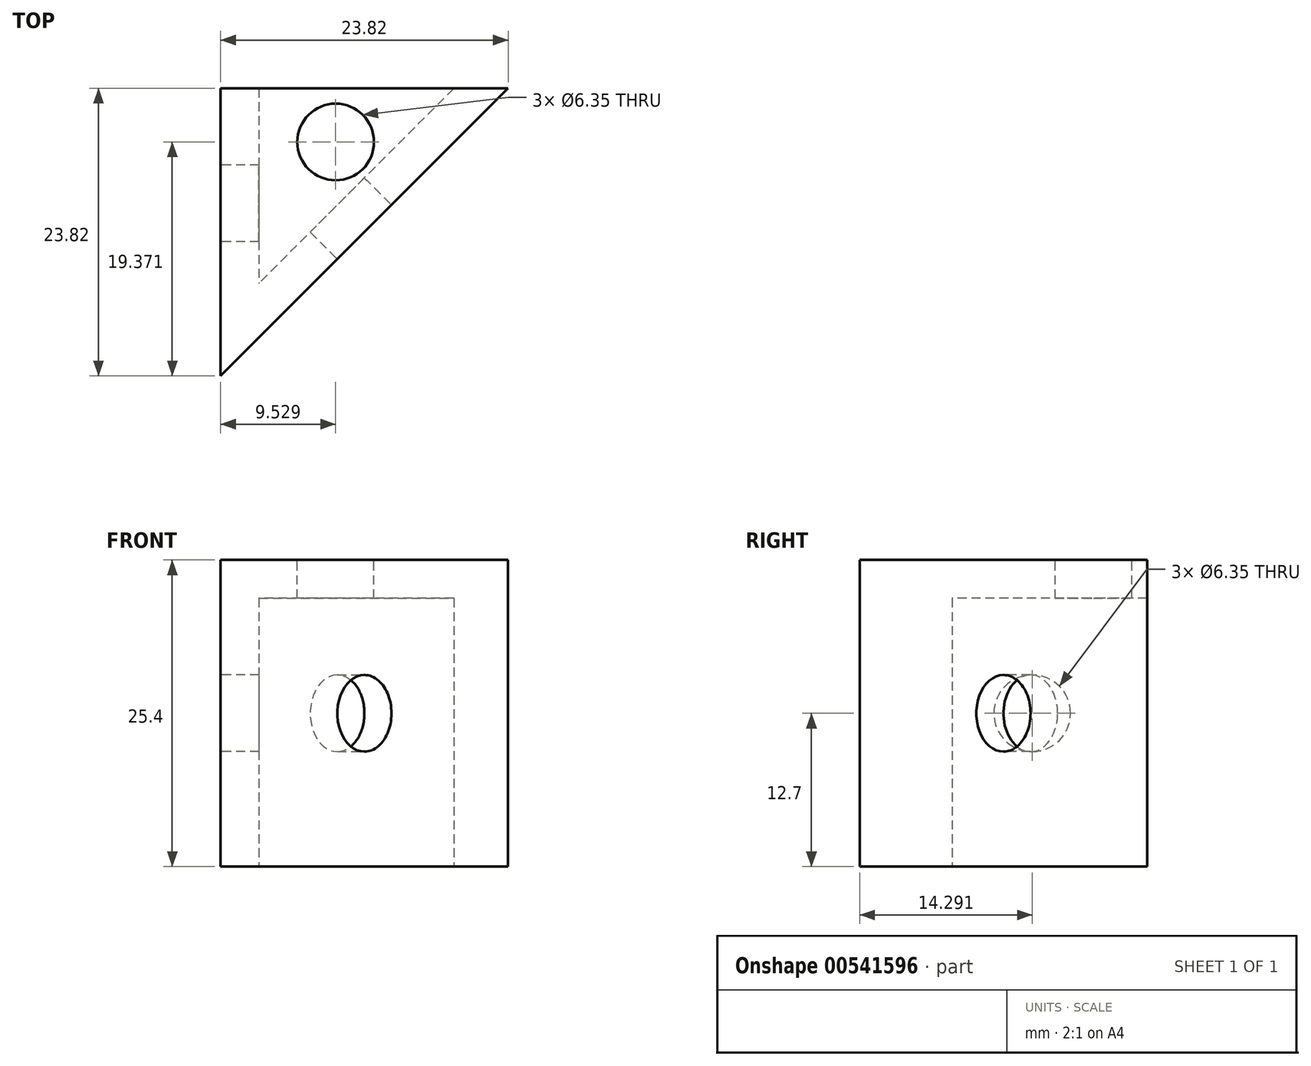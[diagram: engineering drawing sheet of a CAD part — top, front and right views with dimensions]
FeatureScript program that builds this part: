
annotation { "Feature Type Name" : "Feature", "Feature Type Description" : "" }
export const myFeature = defineFeature(function(context is Context, id is Id, definition is map)
    precondition{}
    {
        {
            var Q0;
            Q0=qCreatedBy(makeId("Top.planeOp"),FACE);
            var sketch = newSketch(context, id + "F0", { "sketchPlane" : qUnion([Q0])});
            skLineSegment(sketch, "E0.bottom", {"start": v(-11.9, 11.9) * mm, "end": v(11.9, 11.9) * mm});
            skLineSegment(sketch, "E0.top", {"start": v(-11.9, -11.9) * mm, "end": v(11.9, -11.9) * mm});
            skLineSegment(sketch, "E0.left", {"start": v(-11.9, 11.9) * mm, "end": v(-11.9, -11.9) * mm});
            skLineSegment(sketch, "E0.right", {"start": v(11.9, 11.9) * mm, "end": v(11.9, -11.9) * mm});
            skPoint(sketch, "E0.middle", {"position": v(0, 0) * mm});
            skLineSegment(sketch, "E1", {"start": v(11.9, 11.9) * mm, "end": v(-11.9, -11.9) * mm});
            skSolve(sketch);
        }
        {
            var Q0;
            Q0=makeQuery(id+"F0.imprint","IMPRINT",FACE,{"disambiguationData":[TD([[makeQuery(id+"F0.imprint","IMPRINT",EDGE,{"derivedFrom":sQuery(id+"F0.wireOp",EDGE,"E0.bottom")}),-1.0]])]});
            extrude(context, id + "F1", {"entities" : qUnion([Q0]), "depth" : 25.4 * mm, "offsetDistance" : 25.4 * mm});
        }
        {
            var Q0;
            Q0=makeQuery(id+"F1.opExtrude","SWEPT_FACE",FACE,{"disambiguationData":[OSD([sQuery(id+"F0.wireOp",EDGE,"E0.bottom")])]});
            shell(context, id + "F2", {"entities" : qUnion([Q0]), "thickness" : 3.17 * mm});
        }
        {
            var Q0;
            {var subQ0=sQuery(id+"F0.wireOp",EDGE,"E1");var subQ1=sQuery(id+"F0.wireOp",EDGE,"E0.left");var subQ2=sQuery(id+"F0.wireOp",EDGE,"E0.bottom");Q0=makeQuery(id+"F2.opShell","OFFSET_FACE",FACE,{"disambiguationData":[OSD([subQ2,subQ1,subQ0]),TDD([makeQuery(id+"F1.opExtrude","CAP_FACE",FACE,{"disambiguationData":[OSD([subQ2,subQ1,subQ0])],"isStart":true})])]});}
            extrude(context, id + "F3", {"entities" : qUnion([Q0]), "operationType" : NewBodyOperationType.REMOVE, "oppositeDirection" : true, "depth" : 25.4 * mm, "offsetDistance" : 25.4 * mm});
        }
        {
            var Q0;
            Q0=makeQuery(id+"F1.opExtrude","SWEPT_FACE",FACE,{"disambiguationData":[OSD([sQuery(id+"F0.wireOp",EDGE,"E0.left")])]});
            var sketch = newSketch(context, id + "F4", { "sketchPlane" : qUnion([Q0])});
            skCircle(sketch, "E2", {"center": v(-2.38, 12.7) * mm, "radius": 3.18 * mm});
            skSolve(sketch);
        }
        {
            var Q0;
            Q0=makeQuery(id+"F4.imprint","IMPRINT",FACE,{"disambiguationData":[TD([[makeQuery(id+"F4.imprint","IMPRINT",EDGE,{"derivedFrom":sQuery(id+"F4.wireOp",EDGE,"E2")}),1.0]])]});
            extrude(context, id + "F5", {"entities" : qUnion([Q0]), "operationType" : NewBodyOperationType.REMOVE, "oppositeDirection" : true, "depth" : 3.17 * mm, "offsetDistance" : 25.4 * mm});
        }
        {
            var Q0;
            Q0=makeQuery(id+"F1.opExtrude","CAP_FACE",FACE,{"disambiguationData":[OSD([sQuery(id+"F0.wireOp",EDGE,"E0.bottom"),sQuery(id+"F0.wireOp",EDGE,"E0.left"),sQuery(id+"F0.wireOp",EDGE,"E1")])],"isStart":false});
            var sketch = newSketch(context, id + "F6", { "sketchPlane" : qUnion([Q0])});
            skCircle(sketch, "E3", {"center": v(-2.38, 7.46) * mm, "radius": 3.18 * mm});
            skSolve(sketch);
        }
        {
            var Q0;
            {var subQ0=sQuery(id+"F6.wireOp",EDGE,"E3");var subQ1=sQuery(id+"F6.wireOp",EDGE,"HWwZXyzN-BkNU-UMwY-gXSM-99bSMozpZ1Sp");var subQ2=makeQuery(id+"F6.imprint","INTERSECT",VERTEX,{"disambiguationData":[OD(0.0)],"derivedFrom":[subQ1,subQ0]});Q0=makeQuery(id+"F6.imprint","IMPRINT",FACE,{"disambiguationData":[TD([[makeQuery(id+"F6.imprint","IMPRINT",EDGE,{"disambiguationData":[TD([[subQ2,-1.0]])],"derivedFrom":subQ1}),-1.0]])]});}
            var Q1;
            {var subQ0=sQuery(id+"F6.wireOp",EDGE,"E3");var subQ1=sQuery(id+"F6.wireOp",EDGE,"HWwZXyzN-BkNU-UMwY-gXSM-99bSMozpZ1Sp");var subQ2=makeQuery(id+"F6.imprint","INTERSECT",VERTEX,{"disambiguationData":[OD(0.0)],"derivedFrom":[subQ1,subQ0]});Q1=makeQuery(id+"F6.imprint","IMPRINT",FACE,{"disambiguationData":[TD([[makeQuery(id+"F6.imprint","IMPRINT",EDGE,{"disambiguationData":[TD([[subQ2,-1.0]])],"derivedFrom":subQ1}),1.0]])]});}
            var Q2;
            {var subQ0=sQuery(id+"F6.wireOp",EDGE,"xwTGamvL-BoM2-GFio-XRPn-19hndFO4djhj");var subQ1=sQuery(id+"F6.wireOp",EDGE,"HWwZXyzN-BkNU-UMwY-gXSM-99bSMozpZ1Sp");var subQ2=makeQuery(id+"F6.imprint","INTERSECT",VERTEX,{"derivedFrom":[subQ1,subQ0]});Q2=makeQuery(id+"F6.imprint","IMPRINT",FACE,{"disambiguationData":[TD([[makeQuery(id+"F6.imprint","IMPRINT",EDGE,{"disambiguationData":[TD([[subQ2,-1.0]])],"derivedFrom":subQ1}),-1.0]])]});}
            var Q3;
            {var subQ0=sQuery(id+"F6.wireOp",EDGE,"xwTGamvL-BoM2-GFio-XRPn-19hndFO4djhj");var subQ1=sQuery(id+"F6.wireOp",EDGE,"HWwZXyzN-BkNU-UMwY-gXSM-99bSMozpZ1Sp");var subQ2=makeQuery(id+"F6.imprint","INTERSECT",VERTEX,{"derivedFrom":[subQ1,subQ0]});Q3=makeQuery(id+"F6.imprint","IMPRINT",FACE,{"disambiguationData":[TD([[makeQuery(id+"F6.imprint","IMPRINT",EDGE,{"disambiguationData":[TD([[subQ2,-1.0]])],"derivedFrom":subQ1}),1.0]])]});}
            var Q4;
            Q4=makeQuery(id+"F6.imprint","IMPRINT",FACE,{"disambiguationData":[TD([[makeQuery(id+"F6.imprint","IMPRINT",EDGE,{"derivedFrom":sQuery(id+"F6.wireOp",EDGE,"E3")}),1.0]])]});
            extrude(context, id + "F7", {"entities" : qUnion([Q0, Q1, Q2, Q3, Q4]), "operationType" : NewBodyOperationType.REMOVE, "oppositeDirection" : true, "depth" : 25.4 * mm, "offsetDistance" : 25.4 * mm});
        }
        {
            var Q0;
            Q0=makeQuery(id+"F1.opExtrude","SWEPT_FACE",FACE,{"disambiguationData":[OSD([sQuery(id+"F0.wireOp",EDGE,"E1")])]});
            var sketch = newSketch(context, id + "F8", { "sketchPlane" : qUnion([Q0])});
            skLineSegment(sketch, "E4", {"start": v(-16.84, 25.4) * mm, "end": v(16.84, 0) * mm});
            skCircle(sketch, "E5", {"center": v(0, 12.7) * mm, "radius": 3.18 * mm});
            skSolve(sketch);
        }
        {
            var Q0;
            {var subQ0=sQuery(id+"F8.wireOp",EDGE,"E5");var subQ1=sQuery(id+"F8.wireOp",EDGE,"E4");var subQ2=makeQuery(id+"F8.imprint","INTERSECT",VERTEX,{"disambiguationData":[OD(0.0)],"derivedFrom":[subQ1,subQ0]});Q0=makeQuery(id+"F8.imprint","IMPRINT",FACE,{"disambiguationData":[TD([[makeQuery(id+"F8.imprint","IMPRINT",EDGE,{"disambiguationData":[TD([[subQ2,-1.0]])],"derivedFrom":subQ1}),1.0]])]});}
            var Q1;
            {var subQ0=sQuery(id+"F8.wireOp",EDGE,"E5");var subQ1=sQuery(id+"F8.wireOp",EDGE,"E4");var subQ2=makeQuery(id+"F8.imprint","INTERSECT",VERTEX,{"disambiguationData":[OD(0.0)],"derivedFrom":[subQ1,subQ0]});Q1=makeQuery(id+"F8.imprint","IMPRINT",FACE,{"disambiguationData":[TD([[makeQuery(id+"F8.imprint","IMPRINT",EDGE,{"disambiguationData":[TD([[subQ2,-1.0]])],"derivedFrom":subQ1}),-1.0]])]});}
            extrude(context, id + "F9", {"entities" : qUnion([Q0, Q1]), "operationType" : NewBodyOperationType.REMOVE, "oppositeDirection" : true, "depth" : 3.17 * mm, "offsetDistance" : 25.4 * mm});
        }
    });
